# Revit family: MT-HB_SLIDING DOOR_XXXX
name_source: partatom
category: Doors
revit_build: Autodesk Revit 2017 (Build: 20160225_1515(x64)
units: mm (PartAtom-declared; Revit-internal decimal feet)

## family parameters
Always vertical = Yes
Cut with Voids When Loaded = No
Host = Wall
OmniClass Number = 23.30.20.00
OmniClass Title = Windows
Room Calculation Point = No
Shared = No

## types (1)
- XXXX
    A = 75 mm  [stored 0.246063 ft]
    AIR POCKET = 8 mm  [stored 0.0262467 ft]
    ANZRC COMPLIANT = YES
    Analytic Construction = <None>
    BOT PANEL POSITION = 35 mm  [stored 0.114829 ft]
    DOUBLE GLAZED = Yes
    DOUBLE GLAZED THICKNESS = 18 mm  [stored 0.0590551 ft]
    Default Sill Height = 0 mm  [stored 0 ft]
    FRAME MATERIAL = <By Category>
    GLAZED MATERIAL = Glass
    Height = 2700 mm  [stored 8.85827 ft]
    MAX HEIGHT = 3000 mm  [stored 9.84252 ft]
    MAX PANEL HEIGHT = 3000 mm  [stored 9.84252 ft]
    MAX PANEL WIDTH = 1250 mm  [stored 4.10105 ft]
    MAX WIDTH = 4000 mm  [stored 13.1234 ft]
    Manufacturer = ALSPEC
    Model = HAWKESBURY TOP HUNG COMMERCIAL SLIDING DOOR
    OFFSET = 10 mm  [stored 0.0328084 ft]
    OVERALL FRAME HEIGHT = 2700 mm  [stored 8.85827 ft]
    OVERALL FRAME WIDTH = 3500 mm  [stored 11.4829 ft]
    PANEL HEIGHT = 2590 mm  [stored 8.49738 ft]
    PANEL WIDTH = 913 mm
    Rough Height = 2700 mm  [stored 8.85827 ft]
    Rough Width = 3500 mm  [stored 11.4829 ft]
    SINGLE GLAZED THICKNESS = 5 mm  [stored 0.0164042 ft]
    TOLERANCE = 0 mm  [stored 0 ft]
    TOP PANEL POSITION = 2574 mm  [stored 8.44488 ft]
    URL = WWW.ALSPEC.COM.AU
    VERSION = 2.1
    WARNING = No
    Wall Closure = By host
    Width = 3500 mm  [stored 11.4829 ft]
    YEAR = 2019

note: [stored X ft] marks values corroborated as IEEE doubles in the binary element streams (Revit-internal decimal feet)

## geometry (parser evidence)
native form markers: Extrusion x1, Sweep x46
no freeform markers — native parametric forms only
